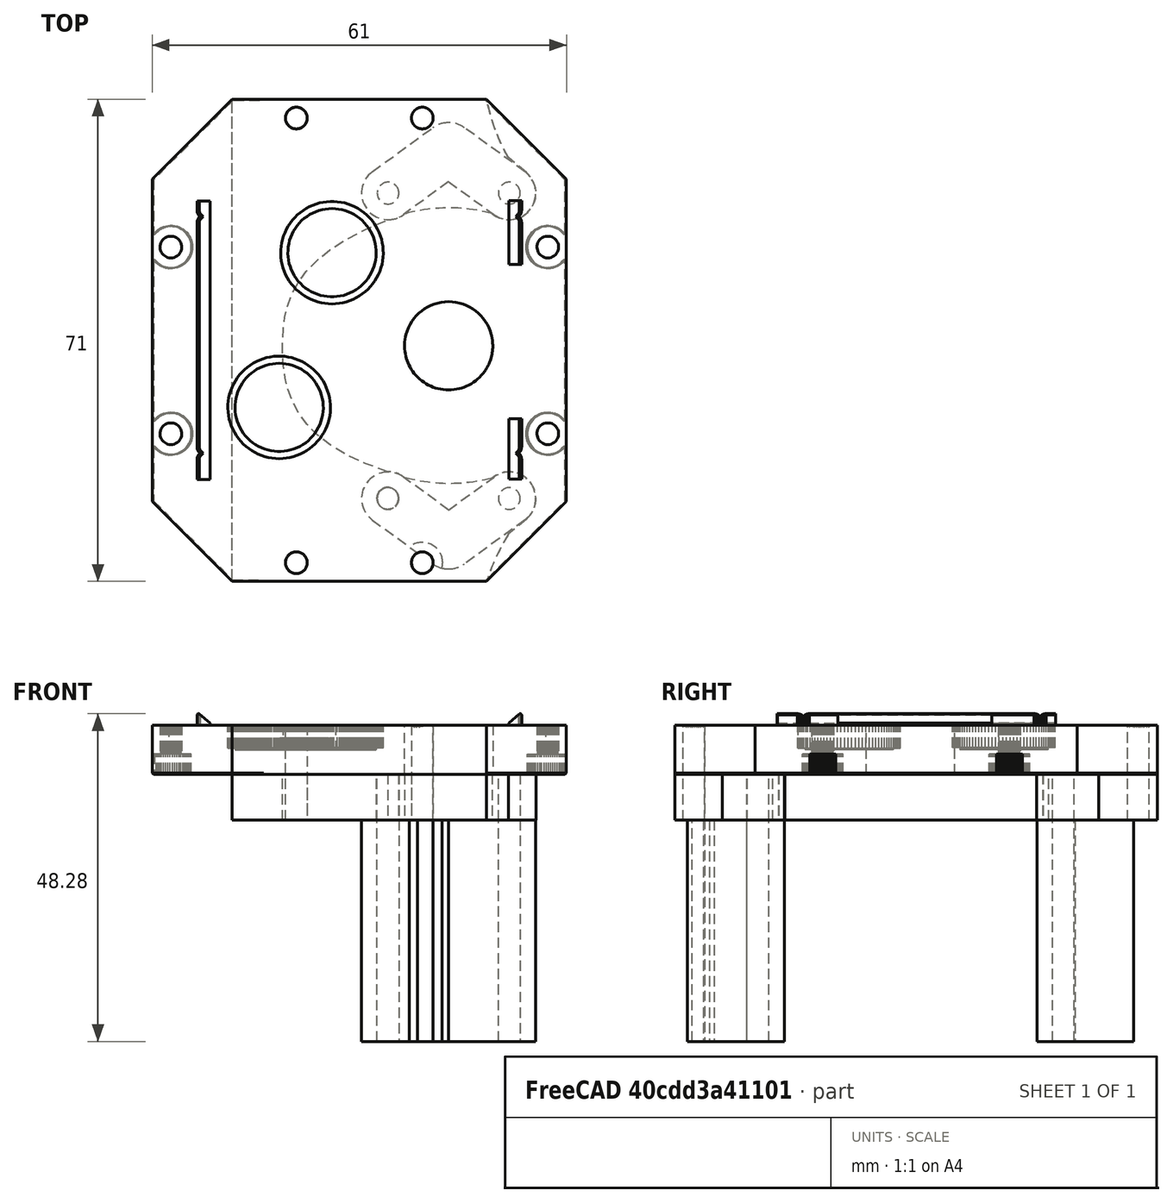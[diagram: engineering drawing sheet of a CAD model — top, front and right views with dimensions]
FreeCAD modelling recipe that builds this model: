
FCSTD DOCUMENT  (FreeCAD 0.20R29177 (Git))
Label: frontplate
License: All rights reserved
LicenseURL: http://en.wikipedia.org/wiki/All_rights_reserved
objects: Sketcher::SketchObject×13, PartDesign::Pad×7, PartDesign::Pocket×6, PartDesign::FeatureBase×4, PartDesign::Body×4, Part::Feature×2, Mesh::Feature×1, Spreadsheet::Sheet×1, App::Part×1
note: 49 computed .brp shape members not serialized (recipe doc carries the construction recipe); baked Part::Feature solids carry a one-line shape summary decoded from their .brp

FEATURE [Mesh::Feature] Gearbox_Housing___front  label="Gearbox Housing - front"
FEATURE [Part::Feature] Gearbox_Housing___front001001_solid  label="Gearbox_Housing___front001001 (Solid)"
  shape: bbox 61 x 71 x 8.923 mm, 6491 faces (baked)
FEATURE [PartDesign::FeatureBase] BaseFeature
  BaseFeature = -> Gearbox_Housing___front001001_solid
FEATURE [Sketcher::SketchObject] Sketch  label="SketchScoketHole"
  ExternalGeometry = -> [BaseFeature]
  FullyConstrained = true
  MapMode = 5
  Placement = pos=(0,0,7.23558) rot=(0,0,1;0rad)
  Support = -> [BaseFeature]
  expr: Constraints[0] = Spreadsheet.xFromLower
  expr: Constraints[1] = Spreadsheet.cy
  expr: Constraints[2] = Spreadsheet.clR + Spreadsheet.clSpacing
  sketch-geometry (1):
    g0: Circle CenterX=56.727 CenterY=51.9969 CenterZ=0 NormalX=0 NormalY=0 NormalZ=1 AngleXU=0 Radius=6.5
  constraints (3):
    c: DistanceY(g-3,g0) = 34.7
    c: DistanceX(g-4,g0) = 43.65
    c: Radius(g0) = 6.5
FEATURE [Spreadsheet::Sheet] Spreadsheet
  cells = A2=xFromLower; B2(xFromLower)=34.7; A3=cy; B3(cy)=43.65; A4=clR; B4(clR)=5; A5=clSpacing; B5(clSpacing)=1.5; A6=motorHolderX; B6(motorHolderX)=22.5; A7=motorHolderY; B7(motorHolderY)=8.93; A8=screwHoleR; B8(screwHoleR)=1.6; A9=tightScrewHoleR; B9(tightScrewHoleR)=1.38
FEATURE [Sketcher::SketchObject] Sketch001  label="SketchBigHole"
  FullyConstrained = false
  MapMode = 5
  Placement = pos=(0,0,7.23558) rot=(0,0,1;0rad)
  Support = -> [BaseFeature]
  sketch-geometry (1):
    g0: Circle CenterX=53.4583 CenterY=50.1454 CenterZ=0 NormalX=0 NormalY=0 NormalZ=1 AngleXU=0 Radius=13.1285
FEATURE [PartDesign::Pad] Pad  label="PadBigHole"
  BaseFeature = -> BaseFeature
  Direction = (0,0,1)
  Length = 10
  Length2 = 10
  Profile = -> Sketch001
  ReferenceAxis = -> Sketch001 [N_Axis]
  Type = 3
  UpToFace = -> BaseFeature [Face97]
FEATURE [Sketcher::SketchObject] Sketch002  label="Sketch3SmallHole"
  FullyConstrained = false
  MapMode = 5
  Placement = pos=(0,0,7.23558) rot=(0,0,1;0rad)
  Support = -> [Pad]
  sketch-geometry (4):
    g0: LineSegment StartX=48.3223 StartY=67.3363 StartZ=0 EndX=68.1146 EndY=67.3363 EndZ=0
    g1: LineSegment StartX=68.1146 StartY=67.3363 StartZ=0 EndX=68.1146 EndY=33.6704 EndZ=0
    g2: LineSegment StartX=68.1146 StartY=33.6704 StartZ=0 EndX=48.3223 EndY=33.6704 EndZ=0
    g3: LineSegment StartX=48.3223 StartY=33.6704 StartZ=0 EndX=48.3223 EndY=67.3363 EndZ=0
  constraints (8):
    c: Coincident(g0,g1)
    c: Coincident(g1,g2)
    c: Coincident(g2,g3)
    c: Coincident(g3,g0)
    c: Horizontal(g0)
    c: Horizontal(g2)
    c: Vertical(g1)
    c: Vertical(g3)
FEATURE [PartDesign::Pad] Pad001
  BaseFeature = -> Pad
  Direction = (0,0,1)
  Length = 10
  Length2 = 10
  Profile = -> Sketch002
  ReferenceAxis = -> Sketch002 [N_Axis]
  Type = 3
  UpToFace = -> Pad [Face3]
FEATURE [Sketcher::SketchObject] Sketch003  label="Sketch2hole"
  FullyConstrained = false
  MapMode = 5
  Placement = pos=(0,0,7.23558) rot=(0,0,1;0rad)
  Support = -> [Pad001]
  sketch-geometry (4):
    g0: LineSegment StartX=37.404 StartY=53.6328 StartZ=0 EndX=69.0593 EndY=53.6328 EndZ=0
    g1: LineSegment StartX=69.0593 StartY=53.6328 StartZ=0 EndX=69.0593 EndY=48.2482 EndZ=0
    g2: LineSegment StartX=69.0593 StartY=48.2482 StartZ=0 EndX=37.404 EndY=48.2482 EndZ=0
    g3: LineSegment StartX=37.404 StartY=48.2482 StartZ=0 EndX=37.404 EndY=53.6328 EndZ=0
  constraints (8):
    c: Coincident(g0,g1)
    c: Coincident(g1,g2)
    c: Coincident(g2,g3)
    c: Coincident(g3,g0)
    c: Horizontal(g0)
    c: Horizontal(g2)
    c: Vertical(g1)
    c: Vertical(g3)
FEATURE [PartDesign::Pad] Pad002
  BaseFeature = -> Pad001
  Direction = (0,0,1)
  Length = 10
  Length2 = 10
  Profile = -> Sketch003
  ReferenceAxis = -> Sketch003 [N_Axis]
  Type = 3
  UpToFace = -> Pad001 [Face3]
FEATURE [Sketcher::SketchObject] Sketch004
  FullyConstrained = false
  MapMode = 5
  Placement = pos=(0,0,7.23558) rot=(0,0,1;0rad)
  Support = -> [Pad002]
  sketch-geometry (4):
    g0: LineSegment StartX=38.2659 StartY=48.5447 StartZ=0 EndX=41.0561 EndY=48.5447 EndZ=0
    g1: LineSegment StartX=41.0561 StartY=48.5447 StartZ=0 EndX=41.0561 EndY=47.0742 EndZ=0
    g2: LineSegment StartX=41.0561 StartY=47.0742 StartZ=0 EndX=38.2659 EndY=47.0742 EndZ=0
    g3: LineSegment StartX=38.2659 StartY=47.0742 StartZ=0 EndX=38.2659 EndY=48.5447 EndZ=0
  constraints (8):
    c: Coincident(g0,g1)
    c: Coincident(g1,g2)
    c: Coincident(g2,g3)
    c: Coincident(g3,g0)
    c: Horizontal(g0)
    c: Horizontal(g2)
    c: Vertical(g1)
    c: Vertical(g3)
FEATURE [PartDesign::Pad] Pad003  label="PadAllHolesDone"
  BaseFeature = -> Pad002
  Direction = (0,0,1)
  Length = 10
  Length2 = 10
  Profile = -> Sketch004
  ReferenceAxis = -> Sketch004 [N_Axis]
  Type = 3
  UpToFace = -> Pad002 [Face3]
FEATURE [PartDesign::Pocket] Pocket
  BaseFeature = -> Pad003
  Direction = (0,0,-1)
  Length = 0
  Length2 = 5
  Profile = -> Sketch
  ReferenceAxis = -> Sketch [N_Axis]
  Type = 3
  UpToFace = -> Pad003 [Face3]
FEATURE [Sketcher::SketchObject] Sketch006  label="SketchPlugSideHole"
  ExternalGeometry = -> [Pocket]
  FullyConstrained = false
  MapMode = 5
  Placement = pos=(0,0,-2.9e-15) rot=(1,0,0;3.14159rad)
  Support = -> [Pocket]
  sketch-geometry (8):
    g0: LineSegment StartX=62.3196 StartY=-17.2969 StartZ=0 EndX=29.4678 EndY=-17.2969 EndZ=0
    g1: LineSegment StartX=29.4678 StartY=-17.2969 StartZ=0 EndX=29.4678 EndY=-23.9319 EndZ=0
    g2: LineSegment StartX=29.4678 StartY=-23.9319 StartZ=0 EndX=62.3196 EndY=-23.9319 EndZ=0
    g3: LineSegment StartX=62.3196 StartY=-23.9319 StartZ=0 EndX=62.3196 EndY=-17.2969 EndZ=0
    g4: LineSegment StartX=62.3196 StartY=-88.2969 StartZ=0 EndX=28.8966 EndY=-88.2969 EndZ=0
    g5: LineSegment StartX=28.8966 StartY=-88.2969 StartZ=0 EndX=28.8966 EndY=-80.4852 EndZ=0
    g6: LineSegment StartX=28.8966 StartY=-80.4852 StartZ=0 EndX=62.3196 EndY=-80.4852 EndZ=0
    g7: LineSegment StartX=62.3196 StartY=-80.4852 StartZ=0 EndX=62.3196 EndY=-88.2969 EndZ=0
  constraints (18):
    c: Coincident(g0,g1)
    c: Coincident(g1,g2)
    c: Coincident(g2,g3)
    c: Coincident(g3,g0)
    c: Horizontal(g0)
    c: Horizontal(g2)
    c: Vertical(g1)
    c: Vertical(g3)
    c: Coincident(g0,g-3)
    c: Coincident(g4,g5)
    c: Coincident(g5,g6)
    c: Coincident(g6,g7)
    c: Coincident(g7,g4)
    c: Horizontal(g4)
    c: Horizontal(g6)
    c: Vertical(g5)
    c: Vertical(g7)
    c: Coincident(g4,g-4)
FEATURE [PartDesign::Pad] Pad004
  BaseFeature = -> Pocket
  Direction = (2e-16,0,-1)
  Length = 7
  Length2 = 10
  Profile = -> Sketch006
  ReferenceAxis = -> Sketch006 [N_Axis]
  Reversed = true
  Type = 0
FEATURE [Sketcher::SketchObject] Sketch005  label="SketchMotorHolder"
  ExternalGeometry = -> [Pocket]
  FullyConstrained = false
  MapMode = 5
  Placement = pos=(0,0,-2.9e-15) rot=(1,0,0;3.14159rad)
  Support = -> [Pad004]
  expr: Constraints[0] = Spreadsheet.cy
  expr: Constraints[1] = Spreadsheet.xFromLower
  expr: Constraints[34] = Spreadsheet.motorHolderX
  expr: Constraints[8] = Spreadsheet.motorHolderY
  sketch-geometry (65):
    g0: Circle CenterX=56.727 CenterY=-51.9969 CenterZ=0 NormalX=0 NormalY=0 NormalZ=1 AngleXU=0 Radius=6.08156
    g1: LineSegment StartX=65.657 StartY=-29.4969 StartZ=0 EndX=47.787 EndY=-29.4969 EndZ=0
    g2: LineSegment StartX=47.787 StartY=-29.4969 StartZ=0 EndX=47.787 EndY=-74.4969 EndZ=0
    g3: LineSegment StartX=65.657 StartY=-74.4969 StartZ=0 EndX=65.657 EndY=-29.4969 EndZ=0
    g4: Circle CenterX=56.727 CenterY=-51.9969 CenterZ=0 NormalX=0 NormalY=0 NormalZ=1 AngleXU=0 Radius=17.5
    g5: ArcOfCircle CenterX=65.657 CenterY=-29.4969 CenterZ=0 NormalX=0 NormalY=0 NormalZ=1 AngleXU=0 Radius=3.93 StartAngle=4.01426 EndAngle=7.15572
    g6: LineSegment StartX=68.1835 StartY=-26.4867 StartZ=0 EndX=65.5511 EndY=-24.2773 EndZ=0
    g7: Circle CenterX=65.657 CenterY=-29.4969 CenterZ=0 NormalX=0 NormalY=0 NormalZ=1 AngleXU=0 Radius=1.6
    g8: LineSegment StartX=56.727 StartY=-51.9969 StartZ=0 EndX=56.727 EndY=-19.7191 EndZ=0
    g9: LineSegment StartX=56.727 StartY=-51.9969 StartZ=0 EndX=61.8338 EndY=-51.9969 EndZ=0
    g10: Circle CenterX=47.7388 CenterY=-29.5399 CenterZ=0 NormalX=0 NormalY=0 NormalZ=1 AngleXU=0 Radius=1.6
    g11: ArcOfCircle CenterX=47.7388 CenterY=-29.5399 CenterZ=0 NormalX=0 NormalY=0 NormalZ=1 AngleXU=0 Radius=3.93 StartAngle=4.72464 EndAngle=5.41052
    g12: LineSegment StartX=47.787 StartY=-74.4969 StartZ=0 EndX=47.787 EndY=-29.4969 EndZ=0
    g13: LineSegment StartX=65.657 StartY=-29.4969 StartZ=0 EndX=65.657 EndY=-74.4969 EndZ=0
    g14: LineSegment StartX=56.727 StartY=-51.9969 StartZ=0 EndX=56.727 EndY=-84.2748 EndZ=0
    g15: Circle CenterX=63.1308 CenterY=-32.5075 CenterZ=0 NormalX=0 NormalY=0 NormalZ=1 AngleXU=0 Radius=1
    g16: Circle CenterX=56.727 CenterY=-30.841 CenterZ=0 NormalX=0 NormalY=0 NormalZ=1 AngleXU=0 Radius=1
    g17: Circle CenterX=50.265 CenterY=-32.5505 CenterZ=0 NormalX=0 NormalY=0 NormalZ=1 AngleXU=0 Radius=1
    g18: BSplineCurve PolesCount=3 KnotsCount=2 Degree=2 IsPeriodic=0
    g19: GeomPoint X=63.1907 Y=-32.5595 Z=0
    g20: GeomPoint X=50.2632 Y=-32.5595 Z=0
    g21: Circle CenterX=65.5511 CenterY=-24.2773 CenterZ=0 NormalX=0 NormalY=0 NormalZ=1 AngleXU=0 Radius=1
    g22: Circle CenterX=63.5507 CenterY=-20.9909 CenterZ=0 NormalX=0 NormalY=0 NormalZ=1 AngleXU=0 Radius=1
    g23: Circle CenterX=62.3196 CenterY=-17.2969 CenterZ=0 NormalX=0 NormalY=0 NormalZ=1 AngleXU=0 Radius=1
    g24: BSplineCurve PolesCount=3 KnotsCount=2 Degree=2 IsPeriodic=0
    g25: GeomPoint X=65.5511 Y=-24.2773 Z=0
    g26: GeomPoint X=62.3196 Y=-17.2969 Z=0
    g27: LineSegment StartX=56.727 StartY=-51.9969 StartZ=0 EndX=18.4605 EndY=-51.9969 EndZ=0
    g28: LineSegment StartX=65.657 StartY=-74.4969 StartZ=0 EndX=47.787 EndY=-74.4969 EndZ=0
    g29: ArcOfCircle CenterX=65.657 CenterY=-74.4969 CenterZ=0 NormalX=0 NormalY=0 NormalZ=1 AngleXU=0 Radius=3.93 StartAngle=5.41065 EndAngle=8.55211
    g30: LineSegment StartX=68.1835 StartY=-77.5071 StartZ=0 EndX=65.5511 EndY=-79.7166 EndZ=0
    g31: Circle CenterX=65.657 CenterY=-74.4969 CenterZ=0 NormalX=0 NormalY=0 NormalZ=1 AngleXU=0 Radius=1.6
    g32: LineSegment StartX=56.727 StartY=-51.9969 StartZ=0 EndX=56.727 EndY=-84.2748 EndZ=0
    g33: LineSegment StartX=56.727 StartY=-51.9969 StartZ=0 EndX=61.8338 EndY=-51.9969 EndZ=0
    g34: Circle CenterX=47.797 CenterY=-74.4969 CenterZ=0 NormalX=0 NormalY=0 NormalZ=1 AngleXU=0 Radius=1.6
    g35: ArcOfCircle CenterX=47.797 CenterY=-74.4969 CenterZ=0 NormalX=0 NormalY=0 NormalZ=1 AngleXU=0 Radius=3.93 StartAngle=0.891823 EndAngle=1.57333
    g36: Circle CenterX=63.1308 CenterY=-71.4864 CenterZ=0 NormalX=0 NormalY=0 NormalZ=1 AngleXU=0 Radius=1
    g37: Circle CenterX=56.727 CenterY=-73.1528 CenterZ=0 NormalX=0 NormalY=0 NormalZ=1 AngleXU=0 Radius=1
    g38: Circle CenterX=50.265 CenterY=-71.4385 CenterZ=0 NormalX=0 NormalY=0 NormalZ=1 AngleXU=0 Radius=1
    g39: BSplineCurve PolesCount=3 KnotsCount=2 Degree=2 IsPeriodic=0
    g40: GeomPoint X=63.1907 Y=-71.4343 Z=0
    g41: GeomPoint X=50.2632 Y=-71.4343 Z=0
    g42: Circle CenterX=65.5511 CenterY=-79.7166 CenterZ=0 NormalX=0 NormalY=0 NormalZ=1 AngleXU=0 Radius=1
    g43: Circle CenterX=63.5507 CenterY=-83.0029 CenterZ=0 NormalX=0 NormalY=0 NormalZ=1 AngleXU=0 Radius=1
    g44: Circle CenterX=62.3196 CenterY=-88.2969 CenterZ=0 NormalX=0 NormalY=0 NormalZ=1 AngleXU=0 Radius=1
    g45: BSplineCurve PolesCount=3 KnotsCount=2 Degree=2 IsPeriodic=0
    g46: GeomPoint X=65.5511 Y=-79.7166 Z=0
    g47: GeomPoint X=62.3196 Y=-88.2969 Z=0
    g48: LineSegment StartX=62.3196 StartY=-17.2969 StartZ=0 EndX=24.8343 EndY=-17.2969 EndZ=0
    g49: LineSegment StartX=24.8343 StartY=-17.2969 StartZ=0 EndX=24.8343 EndY=-88.2969 EndZ=0
    g50: LineSegment StartX=62.3196 StartY=-88.2969 StartZ=0 EndX=24.8343 EndY=-88.2969 EndZ=0
    g51-g55: Circle x5 (B-spline internal-alignment scaffolding for g56; pole/knot coordinates omitted)
    g56: BSplineCurve PolesCount=5 KnotsCount=3 Degree=3 IsPeriodic=0
    g57: GeomPoint X=47.787 Y=-33.4696 Z=0
    g58: GeomPoint X=32.2654 Y=-51.7534 Z=0
    g59: GeomPoint X=47.787 Y=-70.5669 Z=0
    g60: LineSegment StartX=56.727 StartY=-51.9969 StartZ=0 EndX=63.4257 EndY=-60.9226 EndZ=0
    g61: LineSegment StartX=65.657 StartY=-29.4969 StartZ=0 EndX=56.727 EndY=-51.9969 EndZ=0
    g62: LineSegment StartX=56.727 StartY=-51.9969 StartZ=0 EndX=47.7388 EndY=-29.5399 EndZ=0
    g63: LineSegment StartX=56.727 StartY=-51.9969 StartZ=0 EndX=47.797 EndY=-74.4969 EndZ=0
    g64: LineSegment StartX=56.727 StartY=-51.9969 StartZ=0 EndX=65.657 EndY=-74.4969 EndZ=0
  constraints (110):
    c: DistanceX(g-3,g0) = 43.65
    c: DistanceY(g0,g-4) = 34.7
    c: Coincident(g1,g2)
    c: Coincident(g3,g1)
    c: Horizontal(g1)
    c: Vertical(g2)
    c: Vertical(g3)
    c: Distance(g1,g1) = 17.87
    c: DistanceX(g0,g1) = 8.93
    c: Coincident(g4,g0)
    c: Tangent(g5,g6) = -1.5708
    c: Coincident(g6,g24) = -1.5708
    c: Coincident(g5,g1)
    c: Coincident(g7,g5)
    c: Radius(g7) = 1.6
    c: Coincident(g8,g0)
    c: Vertical(g8)
    c: Coincident(g9,g0)
    c: Horizontal(g9)
    c: Coincident(g18,g11) = 1.5708
    c: Coincident(g10,g11)
    c: Radius(g10) = 1.6
    c: Vertical(g12)
    c: Vertical(g13)
    c: Vertical(g14)
    c: Diameter(g4) = 35
    c: Weight(g15) = 1
    c: Coincident(g18,g5)
    c: Equal(g15,g16)
    c: PointOnObject(g16,g8)
    c: Equal(g15,g17)
    c: InternalAlignment(g15,g18)
    c: InternalAlignment(g16,g18)
    c: InternalAlignment(g17,g18)
    c: DistanceY(g0,g5) = 22.5
    c: Radius(g5) = 3.93
    c: Radius(g11) = 3.93
    c: Weight(g21) = 1
    c: Equal(g21,g22)
    c: Equal(g21,g23)
    c: Coincident(g24,g-5)
    c: InternalAlignment(g21,g24)
    c: InternalAlignment(g22,g24)
    c: InternalAlignment(g23,g24)
    c: InternalAlignment(g25,g24)
    c: InternalAlignment(g26,g24)
    c: Horizontal(g27)
    c: PointOnObject(g11,g2)
    c: Coincident(g27,g0)
    c: Horizontal(g28)
    c: Distance(g28,g28) = 17.87
    c: Tangent(g29,g30) = 1.5708
    c: Coincident(g30,g45) = -1.5708
    c: Coincident(g29,g28)
    c: Coincident(g31,g29)
    c: Radius(g31) = 1.6
    c: Vertical(g32)
    c: Horizontal(g33)
    c: Coincident(g39,g35) = -1.5708
    c: Coincident(g34,g35)
    c: Radius(g34) = 1.6
    c: Weight(g36) = 1
    c: Coincident(g39,g29)
    c: Equal(g36,g37)
    c: PointOnObject(g37,g32)
    c: Equal(g36,g38)
    c: InternalAlignment(g36,g39)
    c: InternalAlignment(g37,g39)
    c: InternalAlignment(g38,g39)
    c: Radius(g29) = 3.93
    c: Radius(g35) = 3.93
    c: Weight(g42) = 1
    c: Equal(g42,g43)
    c: Equal(g42,g44)
    c: InternalAlignment(g42,g45)
    c: InternalAlignment(g43,g45)
    c: InternalAlignment(g44,g45)
    c: InternalAlignment(g46,g45)
    c: InternalAlignment(g47,g45)
    c: Coincident(g48,g24)
    c: Coincident(g48,g-6)
    c: Coincident(g49,g48)
    c: Coincident(g49,g-7)
    c: Coincident(g45,g-8)
    c: Coincident(g50,g45)
    c: Coincident(g50,g49)
    c: Weight(g51) = 1
    c: Coincident(g56,g11)
    c: Equal(g51,g52)
    c: Equal(g51,g53)
    c: PointOnObject(g53,g27)
    c: Equal(g51,g54)
    c: Equal(g51,g55)
    c: Coincident(g56,g35)
    c: InternalAlignment(g51-g55 -> g56) x5
    c: InternalAlignment(g57,g56)
    c: InternalAlignment(g58,g56)
    c: InternalAlignment(g59,g56)
    c: DistanceY(g29,g0) = 22.5
    c: DistanceY(g34,g0) = 22.5
    c: DistanceX(g0,g29) = 8.93
    c: DistanceX(g34,g0) = 8.93
    c: Coincident(g60,g0)
    c: Coincident(g61,g5)
    c: Coincident(g61,g0)
    c: Coincident(g62,g10)
    c: Coincident(g63,g61)
    c: Coincident(g63,g34)
    c: Coincident(g64,g61)
    c: Coincident(g64,g29)
FEATURE [PartDesign::Pad] Pad005  label="PadMotorHolderScrewPad"
  BaseFeature = -> Pad004
  Direction = (2e-16,0,-1)
  Length = 6.76
  Length2 = 10
  Profile = -> Sketch005
  ReferenceAxis = -> Sketch005 [N_Axis]
  Type = 0
FEATURE [Sketcher::SketchObject] Sketch007  label="SketchScrewHoles"
  ExternalGeometry = -> [Pad005]
  FullyConstrained = false
  MapMode = 5
  Placement = pos=(1.6e-15,0,-6.76) rot=(1,0,0;3.14159rad)
  Support = -> [Pad005]
  expr: Constraints[0] = Spreadsheet.xFromLower
  expr: Constraints[10] = Spreadsheet.motorHolderY
  expr: Constraints[11] = Spreadsheet.motorHolderY
  expr: Constraints[12] = Spreadsheet.motorHolderY
  expr: Constraints[13] = Spreadsheet.motorHolderY
  expr: Constraints[14] = Spreadsheet.motorHolderX
  expr: Constraints[15] = Spreadsheet.motorHolderX
  expr: Constraints[16] = Spreadsheet.motorHolderX
  expr: Constraints[17] = Spreadsheet.motorHolderX
  expr: Constraints[1] = Spreadsheet.cy
  expr: Constraints[6] = Spreadsheet.screwHoleR
  expr: Constraints[9] = Spreadsheet.screwHoleR
  sketch-geometry (23):
    g0: Circle CenterX=56.727 CenterY=-51.9969 CenterZ=0 NormalX=0 NormalY=0 NormalZ=1 AngleXU=0 Radius=5.30478
    g1: LineSegment StartX=56.727 StartY=-51.9969 StartZ=0 EndX=56.727 EndY=-28.385 EndZ=0
    g2: LineSegment StartX=56.727 StartY=-51.9969 StartZ=0 EndX=34.5379 EndY=-51.9969 EndZ=0
    g3: Circle CenterX=65.657 CenterY=-29.4969 CenterZ=0 NormalX=0 NormalY=0 NormalZ=1 AngleXU=0 Radius=1.6
    g4: Circle CenterX=47.797 CenterY=-29.4969 CenterZ=0 NormalX=0 NormalY=0 NormalZ=1 AngleXU=0 Radius=1.6
    g5: Circle CenterX=47.797 CenterY=-74.4969 CenterZ=0 NormalX=0 NormalY=0 NormalZ=1 AngleXU=0 Radius=1.6
    g6: Circle CenterX=65.657 CenterY=-74.4969 CenterZ=0 NormalX=0 NormalY=0 NormalZ=1 AngleXU=0 Radius=1.6
    g7: ArcOfCircle CenterX=65.657 CenterY=-29.4969 CenterZ=0 NormalX=0 NormalY=0 NormalZ=1 AngleXU=0 Radius=3.89911 StartAngle=4.08223 EndAngle=7.22382
    g8: ArcOfCircle CenterX=56.789 CenterY=-23.029 CenterZ=0 NormalX=0 NormalY=0 NormalZ=1 AngleXU=0 Radius=3.89911 StartAngle=0.940636 EndAngle=1.5867
    g9: LineSegment StartX=67.9546 StartY=-26.3467 StartZ=0 EndX=59.0866 EndY=-19.8788 EndZ=0
    g10: LineSegment StartX=56.727 StartY=-27.8098 StartZ=0 EndX=63.3593 EndY=-32.6471 EndZ=0
    g11: ArcOfCircle CenterX=56.789 CenterY=-80.9649 CenterZ=0 NormalX=0 NormalY=0 NormalZ=1 AngleXU=0 Radius=3.89911 StartAngle=4.69648 EndAngle=5.34255
    g12: LineSegment StartX=67.9546 StartY=-77.6471 StartZ=0 EndX=59.0866 EndY=-84.1151 EndZ=0
    g13: ArcOfCircle CenterX=65.657 CenterY=-74.4969 CenterZ=0 NormalX=0 NormalY=0 NormalZ=1 AngleXU=0 Radius=3.89911 StartAngle=5.34255 EndAngle=8.48414
    g14: LineSegment StartX=56.727 StartY=-76.1841 StartZ=0 EndX=63.3593 EndY=-71.3467 EndZ=0
    g15: LineSegment StartX=45.4993 StartY=-26.3467 StartZ=0 EndX=54.3673 EndY=-19.8788 EndZ=0
    g16: ArcOfCircle CenterX=56.6649 CenterY=-23.029 CenterZ=0 NormalX=0 NormalY=0 NormalZ=1 AngleXU=0 Radius=3.89911 StartAngle=1.55489 EndAngle=2.20096
    g17: LineSegment StartX=56.727 StartY=-27.8098 StartZ=0 EndX=50.0946 EndY=-32.6471 EndZ=0
    g18: ArcOfCircle CenterX=47.797 CenterY=-29.4969 CenterZ=0 NormalX=0 NormalY=0 NormalZ=1 AngleXU=0 Radius=3.89911 StartAngle=2.20096 EndAngle=5.34255
    g19: ArcOfCircle CenterX=47.797 CenterY=-74.4969 CenterZ=0 NormalX=0 NormalY=0 NormalZ=1 AngleXU=0 Radius=3.89911 StartAngle=0.940636 EndAngle=4.08223
    g20: LineSegment StartX=45.4993 StartY=-77.6471 StartZ=0 EndX=54.3673 EndY=-84.1151 EndZ=0
    g21: LineSegment StartX=56.727 StartY=-76.1841 StartZ=0 EndX=50.0946 EndY=-71.3467 EndZ=0
    g22: ArcOfCircle CenterX=56.6649 CenterY=-80.9649 CenterZ=0 NormalX=0 NormalY=0 NormalZ=1 AngleXU=0 Radius=3.89911 StartAngle=4.08223 EndAngle=4.7283
  constraints (39):
    c: DistanceY(g0,g-4) = 34.7
    c: DistanceX(g-5,g0) = 43.65
    c: Coincident(g1,g0)
    c: Vertical(g1)
    c: Coincident(g2,g1)
    c: Horizontal(g2)
    c: Radius(g3) = 1.6
    c: Equal(g4,g5)
    c: Equal(g4,g6)
    c: Radius(g4) = 1.6
    c: DistanceX(g0,g3) = 8.93
    c: DistanceX(g4,g0) = 8.93
    c: DistanceX(g5,g0) = 8.93
    c: DistanceX(g0,g6) = 8.93
    c: DistanceY(g0,g3) = 22.5
    c: DistanceY(g0,g4) = 22.5
    c: DistanceY(g5,g0) = 22.5
    c: DistanceY(g6,g0) = 22.5
    c: Tangent(g7,g9) = -1.5708
    c: Tangent(g9,g8) = -1.5708
    c: Tangent(g10,g7) = -1.5708
    c: Equal(g7,g8)
    c: Coincident(g7,g3)
    c: Tangent(g13,g12) = 1.5708
    c: Tangent(g12,g11) = 1.5708
    c: Tangent(g14,g13) = 1.5708
    c: Equal(g13,g11)
    c: Tangent(g18,g15) = 1.5708
    c: Tangent(g15,g16) = 1.5708
    c: Tangent(g17,g18) = 1.5708
    c: Equal(g18,g16)
    c: Tangent(g19,g20) = -1.5708
    c: Tangent(g20,g22) = -1.5708
    c: Tangent(g21,g19) = -1.5708
    c: Equal(g19,g22)
    c: Coincident(g8,g16)
    c: Coincident(g10,g17)
    c: Coincident(g14,g21)
    c: Coincident(g22,g11)
FEATURE [PartDesign::Pad] Pad006
  BaseFeature = -> Pad005
  Direction = (2e-16,0,-1)
  Length = 32.6
  Length2 = 10
  Profile = -> Sketch007
  ReferenceAxis = -> Sketch007 [N_Axis]
  Type = 0
  expr: Length = 32.6mm
FEATURE [Sketcher::SketchObject] Sketch008
  ExternalGeometry = -> [Pad006]
  FullyConstrained = true
  MapMode = 5
  Placement = pos=(0,0,7.23558) rot=(0,0,1;0rad)
  Support = -> [Pad006]
  expr: Constraints[0] = Spreadsheet.screwHoleR
  expr: Constraints[3] = Spreadsheet.screwHoleR
  expr: Constraints[4] = Spreadsheet.screwHoleR
  expr: Constraints[5] = Spreadsheet.screwHoleR
  sketch-geometry (4):
    g0: Circle CenterX=34.2993 CenterY=85.5469 CenterZ=0 NormalX=0 NormalY=0 NormalZ=1 AngleXU=0 Radius=1.6
    g1: Circle CenterX=52.8546 CenterY=85.5469 CenterZ=0 NormalX=0 NormalY=0 NormalZ=1 AngleXU=0 Radius=1.6
    g2: Circle CenterX=34.2993 CenterY=20.0469 CenterZ=0 NormalX=0 NormalY=0 NormalZ=1 AngleXU=0 Radius=1.6
    g3: Circle CenterX=52.8546 CenterY=20.0469 CenterZ=0 NormalX=0 NormalY=0 NormalZ=1 AngleXU=0 Radius=1.6
  constraints (12):
    c: Radius(g0) = 1.6
    c: DistanceY(g0,g-3) = 2.75
    c: DistanceX(g-3,g0) = 9.465
    c: Radius(g1) = 1.6
    c: Radius(g2) = 1.6
    c: Radius(g3) = 1.6
    c: DistanceY(g1,g-3) = 2.75
    c: DistanceY(g-4,g2) = 2.75
    c: DistanceY(g-4,g3) = 2.75
    c: DistanceX(g-4,g2) = 9.465
    c: DistanceX(g3,g-4) = 9.465
    c: DistanceX(g1,g-3) = 9.465
FEATURE [PartDesign::Pocket] Pocket001
  BaseFeature = -> Pad006
  Direction = (0,0,-1)
  Length = 20
  Length2 = 5
  Profile = -> Sketch008
  ReferenceAxis = -> Sketch008 [N_Axis]
  Type = 0
FEATURE [Sketcher::SketchObject] Sketch010  label="SketchLastScrewHole"
  ExternalGeometry = -> [Pocket001]
  FullyConstrained = true
  MapMode = 5
  Placement = pos=(9.1e-15,0,-39.36) rot=(1,0,0;3.14159rad)
  Support = -> [Pocket001]
  expr: Constraints[0] = Spreadsheet.screwHoleR
  sketch-geometry (1):
    g0: Circle CenterX=52.8546 CenterY=-20.0469 CenterZ=0 NormalX=0 NormalY=0 NormalZ=1 AngleXU=0 Radius=1.6
  constraints (3):
    c: Radius(g0) = 1.6
    c: DistanceY(g0,g-3) = 2.75
    c: DistanceX(g0,g-3) = 9.465
FEATURE [PartDesign::Pocket] Pocket002  label="PocketLastScrewHole"
  BaseFeature = -> Pocket001
  Direction = (-2e-16,0,1)
  Length = 5
  Length2 = 5
  Profile = -> Sketch010
  ReferenceAxis = -> Sketch010 [N_Axis]
  Type = 1
FEATURE [Sketcher::SketchObject] Sketch011  label="SketchLastScrewHoleHead"
  ExternalGeometry = -> [Pocket002]
  FullyConstrained = true
  MapMode = 5
  Placement = pos=(9.1e-15,0,-39.36) rot=(1,0,0;3.14159rad)
  Support = -> [Pocket002]
  sketch-geometry (1):
    g0: Circle CenterX=52.8546 CenterY=-20.0469 CenterZ=0 NormalX=0 NormalY=0 NormalZ=1 AngleXU=0 Radius=3
  constraints (3):
    c: Diameter(g0) = 6
    c: DistanceY(g0,g-3) = 2.75
    c: DistanceX(g0,g-3) = 9.465
FEATURE [PartDesign::Body] Body
  BaseFeature = -> Gearbox_Housing___front001001_solid
  Group = -> [BaseFeature,Sketch,Sketch001,Pad,Sketch002,Pad001,Sketch003,Pad002,Sketch004,Pad003,Pocket,Sketch005,Sketch006,Pad004,Pad005,Sketch007,Pad006,Sketch008,Pocket001,Sketch010,Pocket002,Sketch011]
  Origin = -> Origin
  Tip = -> Pocket002
FEATURE [PartDesign::Pocket] Pocket003
  BaseFeature = -> Pocket002
  Direction = (-2e-16,0,1)
  Length = 32.6
  Length2 = 5
  Profile = -> Sketch011
  ReferenceAxis = -> Sketch011 [N_Axis]
  Type = 0
FEATURE [Part::Feature] Pocket003001  label="ShapeAll"
  shape: bbox 61 x 71 x 38.28 mm, 4481 faces (baked)
FEATURE [PartDesign::FeatureBase] BaseFeature002
  BaseFeature = -> Pocket003001
FEATURE [Sketcher::SketchObject] Sketch013
  FullyConstrained = false
  MapMode = 5
  Placement = pos=(0,0,-2.9e-15) rot=(1,0,0;3.14159rad)
  Support = -> [BaseFeature002]
  sketch-geometry (1):
    g0: Circle CenterX=40.2759 CenterY=-51.3362 CenterZ=0 NormalX=0 NormalY=0 NormalZ=1 AngleXU=0 Radius=49.5639
FEATURE [PartDesign::Pocket] Pocket003003
  BaseFeature = -> BaseFeature002
  Direction = (-2e-16,0,1)
  Length = 35
  Length2 = 5
  Profile = -> Sketch013
  ReferenceAxis = -> Sketch013 [N_Axis]
  Reversed = true
  Type = 0
FEATURE [PartDesign::Body] Body002
  BaseFeature = -> Pocket003001
  Group = -> [BaseFeature002,Sketch013,Pocket003003]
  Origin = -> Origin002
  Tip = -> Pocket003003
FEATURE [PartDesign::FeatureBase] BaseFeature003
  BaseFeature = -> Pocket003
FEATURE [PartDesign::FeatureBase] BaseFeature004
  BaseFeature = -> Body
FEATURE [PartDesign::Body] Pocket003Body
  BaseFeature = -> Body
  Group = -> [BaseFeature004]
  Origin = -> Origin004
  Tip = -> BaseFeature004
FEATURE [App::Part] Part
  Group = -> [Pocket003Body]
  Origin = -> Origin003
FEATURE [Sketcher::SketchObject] Sketch014
  FullyConstrained = false
  MapMode = 5
  Placement = pos=(0,0,-2.9e-15) rot=(1,0,0;3.14159rad)
  Support = -> [BaseFeature003]
  sketch-geometry (1):
    g0: Circle CenterX=33.9671 CenterY=-47.4022 CenterZ=0 NormalX=0 NormalY=0 NormalZ=1 AngleXU=0 Radius=57.4404
FEATURE [PartDesign::Pocket] Pocket003004
  BaseFeature = -> BaseFeature003
  Direction = (-2e-16,0,1)
  Length = 150
  Length2 = 5
  Profile = -> Sketch014
  ReferenceAxis = -> Sketch014 [N_Axis]
  Type = 0
FEATURE [PartDesign::Body] Body001  label="BodyMotorHolder"
  BaseFeature = -> Pocket003
  Group = -> [BaseFeature003,Sketch014,Pocket003004]
  Origin = -> Origin001
  Tip = -> Pocket003004
